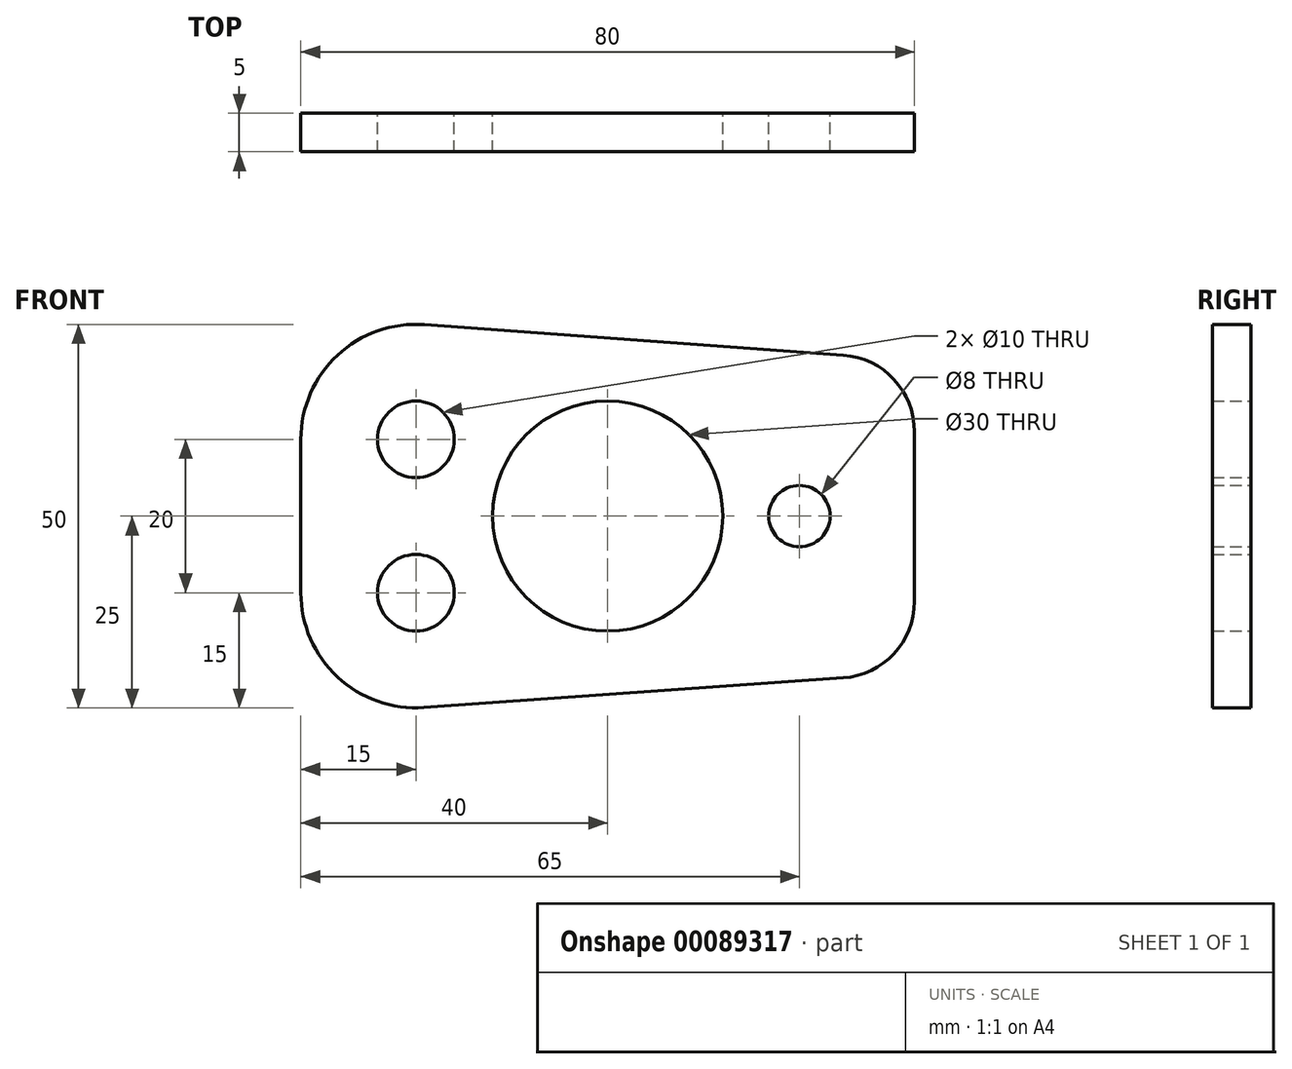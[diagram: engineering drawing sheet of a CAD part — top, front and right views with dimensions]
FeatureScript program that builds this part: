
annotation { "Feature Type Name" : "Feature", "Feature Type Description" : "" }
export const myFeature = defineFeature(function(context is Context, id is Id, definition is map)
    precondition{}
    {
        {
            var Q0;
            Q0=qCreatedBy(makeId("Front.planeOp"),FACE);
            var sketch = newSketch(context, id + "F0", { "sketchPlane" : qUnion([Q0])});
            skLineSegment(sketch, "E0", {"start": v(0, 15) * mm, "end": v(0, -15) * mm, "construction": true});
            skLineSegment(sketch, "E1", {"start": v(40, 0) * mm, "end": v(-40, 0) * mm, "construction": true});
            skCircle(sketch, "E2", {"center": v(-25, 10) * mm, "radius": 5 * mm});
            skCircle(sketch, "E3", {"center": v(-25, -10) * mm, "radius": 5 * mm});
            skArc(sketch, "E4.0", {"start": v(-23.9, 24.96) * mm, "mid": v(-35.21, 20.99) * mm, "end": v(-40, 10) * mm});
            skArc(sketch, "E5.0", {"start": v(-40, -10) * mm, "mid": v(-35.23, -20.97) * mm, "end": v(-23.94, -24.96) * mm});
            skLineSegment(sketch, "E6", {"start": v(-40, 10) * mm, "end": v(-40, -10) * mm});
            skCircle(sketch, "E7", {"center": v(25, 0) * mm, "radius": 4 * mm});
            skArc(sketch, "E8", {"start": v(30.7, -21.1) * mm, "mid": v(37.32, -17.94) * mm, "end": v(40, -11.12) * mm});
            skLineSegment(sketch, "E9", {"start": v(-23.9, 24.96) * mm, "end": v(30.73, 20.98) * mm});
            skLineSegment(sketch, "E10", {"start": v(-23.94, -24.96) * mm, "end": v(30.7, -21.1) * mm});
            skArc(sketch, "E11.trimOffspring", {"start": v(40, 11) * mm, "mid": v(37.32, 17.81) * mm, "end": v(30.73, 20.98) * mm});
            skLineSegment(sketch, "E12", {"start": v(40, 11) * mm, "end": v(40, -11.12) * mm});
            skCircle(sketch, "E13", {"center": v(0, 0) * mm, "radius": 15 * mm});
            skSolve(sketch);
        }
        {
            var Q0;
            Q0 = qSketchRegion(id + "F0", true);
            extrude(context, id + "F1", {"entities" : qUnion([Q0]), "depth" : 5 * mm});
        }
    });
